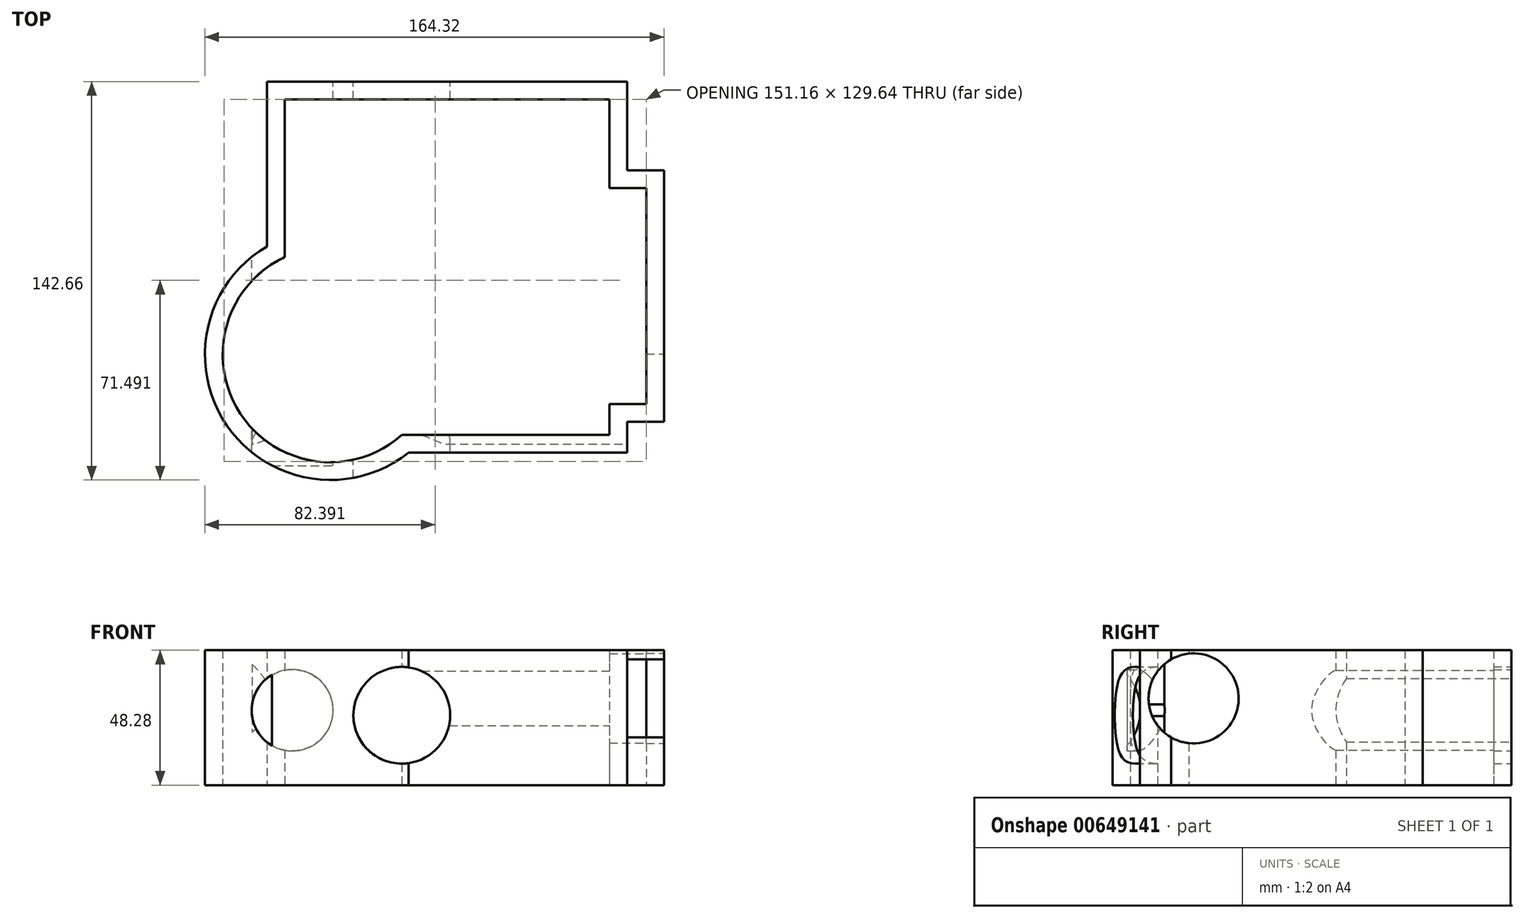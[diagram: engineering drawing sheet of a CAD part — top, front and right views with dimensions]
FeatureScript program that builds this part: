
annotation { "Feature Type Name" : "Feature", "Feature Type Description" : "" }
export const myFeature = defineFeature(function(context is Context, id is Id, definition is map)
    precondition{}
    {
        {
            var Q0;
            Q0=qCreatedBy(makeId("Top.planeOp"),FACE);
            var sketch = newSketch(context, id + "F0", { "sketchPlane" : qUnion([Q0])});
            skLineSegment(sketch, "E0.bottom", {"start": v(-67.34, 73.06) * mm, "end": v(61.57, 73.06) * mm});
            skLineSegment(sketch, "E0.top", {"start": v(-16.65, -59.84) * mm, "end": v(61.57, -59.84) * mm});
            skLineSegment(sketch, "E0.left", {"start": v(-67.34, 73.06) * mm, "end": v(-67.34, 14.02) * mm});
            skLineSegment(sketch, "E0.right", {"start": v(61.57, 73.06) * mm, "end": v(61.57, 41.29) * mm});
            skLineSegment(sketch, "E1.bottom", {"start": v(61.57, 41.29) * mm, "end": v(74.81, 41.29) * mm});
            skLineSegment(sketch, "E1.top", {"start": v(61.57, -48.74) * mm, "end": v(74.81, -48.74) * mm});
            skLineSegment(sketch, "E1.right", {"start": v(74.81, 41.29) * mm, "end": v(74.81, -48.74) * mm});
            skArc(sketch, "E2", {"start": v(-67.34, 14.02) * mm, "mid": v(-81.63, -50.11) * mm, "end": v(-16.65, -59.84) * mm});
            skLineSegment(sketch, "E3.trimOffspring", {"start": v(61.57, -48.74) * mm, "end": v(61.57, -59.84) * mm});
            skLineSegment(sketch, "E4.0", {"start": v(55.22, 66.71) * mm, "end": v(55.22, 34.94) * mm});
            skLineSegment(sketch, "E4.1", {"start": v(-60.99, 66.71) * mm, "end": v(55.22, 66.71) * mm});
            skLineSegment(sketch, "E4.2", {"start": v(55.22, 34.94) * mm, "end": v(68.46, 34.94) * mm});
            skLineSegment(sketch, "E4.3", {"start": v(-60.99, 66.71) * mm, "end": v(-60.99, 10.2) * mm});
            skArc(sketch, "E4.4", {"start": v(-60.99, 10.2) * mm, "mid": v(-76.79, -45.94) * mm, "end": v(-18.96, -53.49) * mm});
            skLineSegment(sketch, "E4.5", {"start": v(68.46, 34.94) * mm, "end": v(68.46, -42.4) * mm});
            skLineSegment(sketch, "E4.6", {"start": v(55.22, -42.4) * mm, "end": v(68.46, -42.4) * mm});
            skLineSegment(sketch, "E4.7", {"start": v(55.22, -42.4) * mm, "end": v(55.22, -53.49) * mm});
            skLineSegment(sketch, "E4.8", {"start": v(-18.96, -53.49) * mm, "end": v(55.22, -53.49) * mm});
            skSolve(sketch);
        }
        {
            var Q0;
            Q0=makeQuery(id+"F0.imprint","IMPRINT",FACE,{"disambiguationData":[TD([[makeQuery(id+"F0.imprint","IMPRINT",EDGE,{"derivedFrom":sQuery(id+"F0.wireOp",EDGE,"E0.bottom")}),-1.0]])]});
            extrude(context, id + "F1", {"entities" : qUnion([Q0]), "depth" : 48.28 * mm, "offsetDistance" : 25.4 * mm});
        }
        {
            var Q0;
            Q0=makeQuery(id+"F1.opExtrude","SWEPT_FACE",FACE,{"disambiguationData":[OSD([sQuery(id+"F0.wireOp",EDGE,"E0.bottom")])]});
            var sketch = newSketch(context, id + "F2", { "sketchPlane" : qUnion([Q0])});
            skCircle(sketch, "E5", {"center": v(19.05, 25) * mm, "radius": 17.33 * mm});
            skSolve(sketch);
        }
        {
            var Q0;
            Q0 = qSketchRegion(id + "F2", true);
            var Q1;
            Q1=makeQuery(id+"F2.imprint","IMPRINT",FACE,{"disambiguationData":[TD([[makeQuery(id+"F2.imprint","IMPRINT",EDGE,{"derivedFrom":sQuery(id+"F2.wireOp",EDGE,"E5")}),1.0]])]});
            extrude(context, id + "F3", {"entities" : qUnion([Q0, Q1]), "operationType" : NewBodyOperationType.REMOVE, "oppositeDirection" : true, "depth" : 178.05 * mm, "offsetDistance" : 25.4 * mm});
        }
        {
            var Q0;
            Q0=makeQuery(id+"F1.opExtrude","SWEPT_FACE",FACE,{"disambiguationData":[OSD([sQuery(id+"F0.wireOp",EDGE,"E1.right")])]});
            var sketch = newSketch(context, id + "F4", { "sketchPlane" : qUnion([Q0])});
            skSolve(sketch);
        }
        {
            var Q0;
            {var subQ0=sQuery(id+"F0.wireOp",EDGE,"E1.right");Q0=makeQuery(id+"F4.imprint","IMPRINT",FACE,{"disambiguationData":[TD([[makeQuery(id+"F4.imprint","IMPRINT",EDGE,{"derivedFrom":makeQuery(id+"F1.opExtrude","CAP_EDGE",EDGE,{"disambiguationData":[OSD([subQ0])],"isStart":true})}),-1.0]])]});}
            var sketch = newSketch(context, id + "F5", { "sketchPlane" : qUnion([Q0])});
            skCircle(sketch, "E6", {"center": v(-40.65, 31.05) * mm, "radius": 16.12 * mm});
            skSolve(sketch);
        }
        {
            var Q0;
            {var subQ0=sQuery(id+"F5.wireOp",EDGE,"E6");var subQ1=makeQuery(id+"F4.imprint","IMPRINT",EDGE,{"derivedFrom":makeQuery(id+"F1.opExtrude","SWEPT_EDGE",EDGE,{"disambiguationData":[OSD([sQuery(id+"F0.wireOp",EDGE,"E1.top"),sQuery(id+"F0.wireOp",EDGE,"E1.right")])]})});var subQ2=makeQuery(id+"F5.imprint","INTERSECT",VERTEX,{"disambiguationData":[OD(0.0)],"derivedFrom":[subQ1,subQ0]});Q0=makeQuery(id+"F5.imprint","IMPRINT",FACE,{"disambiguationData":[TD([[makeQuery(id+"F5.imprint","IMPRINT",EDGE,{"disambiguationData":[TD([[subQ2,-1.0]])],"derivedFrom":subQ0}),1.0]])]});}
            var Q1;
            {var subQ0=sQuery(id+"F5.wireOp",EDGE,"E6");var subQ1=makeQuery(id+"F4.imprint","IMPRINT",EDGE,{"derivedFrom":makeQuery(id+"F1.opExtrude","SWEPT_EDGE",EDGE,{"disambiguationData":[OSD([sQuery(id+"F0.wireOp",EDGE,"E1.top"),sQuery(id+"F0.wireOp",EDGE,"E1.right")])]})});var subQ2=makeQuery(id+"F5.imprint","INTERSECT",VERTEX,{"disambiguationData":[OD(0.0)],"derivedFrom":[subQ1,subQ0]});Q1=makeQuery(id+"F5.imprint","IMPRINT",FACE,{"disambiguationData":[TD([[makeQuery(id+"F5.imprint","IMPRINT",EDGE,{"disambiguationData":[TD([[subQ2,1.0]])],"derivedFrom":subQ0}),1.0]])]});}
            extrude(context, id + "F6", {"entities" : qUnion([Q0, Q1]), "operationType" : NewBodyOperationType.REMOVE, "oppositeDirection" : true, "depth" : 147.46 * mm, "offsetDistance" : 25.4 * mm});
        }
        {
            var Q0;
            Q0=makeQuery(id+"F1.opExtrude","SWEPT_FACE",FACE,{"disambiguationData":[OSD([sQuery(id+"F0.wireOp",EDGE,"E0.bottom")])]});
            var sketch = newSketch(context, id + "F7", { "sketchPlane" : qUnion([Q0])});
            skCircle(sketch, "E7", {"center": v(58.21, 26.8) * mm, "radius": 14.58 * mm});
            skSolve(sketch);
        }
        {
            var Q0;
            {var subQ0=sQuery(id+"F7.wireOp",EDGE,"E7");var subQ1=makeQuery(id+"F1.opExtrude","SWEPT_EDGE",EDGE,{"disambiguationData":[OSD([sQuery(id+"F0.wireOp",EDGE,"E0.bottom"),sQuery(id+"F0.wireOp",EDGE,"E0.left")])]});var subQ2=makeQuery(id+"F7.imprint","INTERSECT",VERTEX,{"disambiguationData":[OD(0.0)],"derivedFrom":[subQ1,subQ0]});Q0=makeQuery(id+"F7.imprint","IMPRINT",FACE,{"disambiguationData":[TD([[makeQuery(id+"F7.imprint","IMPRINT",EDGE,{"disambiguationData":[TD([[subQ2,-1.0]])],"derivedFrom":subQ0}),1.0]])]});}
            var Q1;
            {var subQ0=sQuery(id+"F7.wireOp",EDGE,"E7");var subQ1=makeQuery(id+"F1.opExtrude","SWEPT_EDGE",EDGE,{"disambiguationData":[OSD([sQuery(id+"F0.wireOp",EDGE,"E0.bottom"),sQuery(id+"F0.wireOp",EDGE,"E0.left")])]});var subQ2=makeQuery(id+"F7.imprint","INTERSECT",VERTEX,{"disambiguationData":[OD(0.0)],"derivedFrom":[subQ1,subQ0]});Q1=makeQuery(id+"F7.imprint","IMPRINT",FACE,{"disambiguationData":[TD([[makeQuery(id+"F7.imprint","IMPRINT",EDGE,{"disambiguationData":[TD([[subQ2,1.0]])],"derivedFrom":subQ0}),1.0]])]});}
            extrude(context, id + "F8", {"entities" : qUnion([Q0, Q1]), "operationType" : NewBodyOperationType.REMOVE, "oppositeDirection" : true, "depth" : 137.54 * mm, "offsetDistance" : 25.4 * mm});
        }
    });
